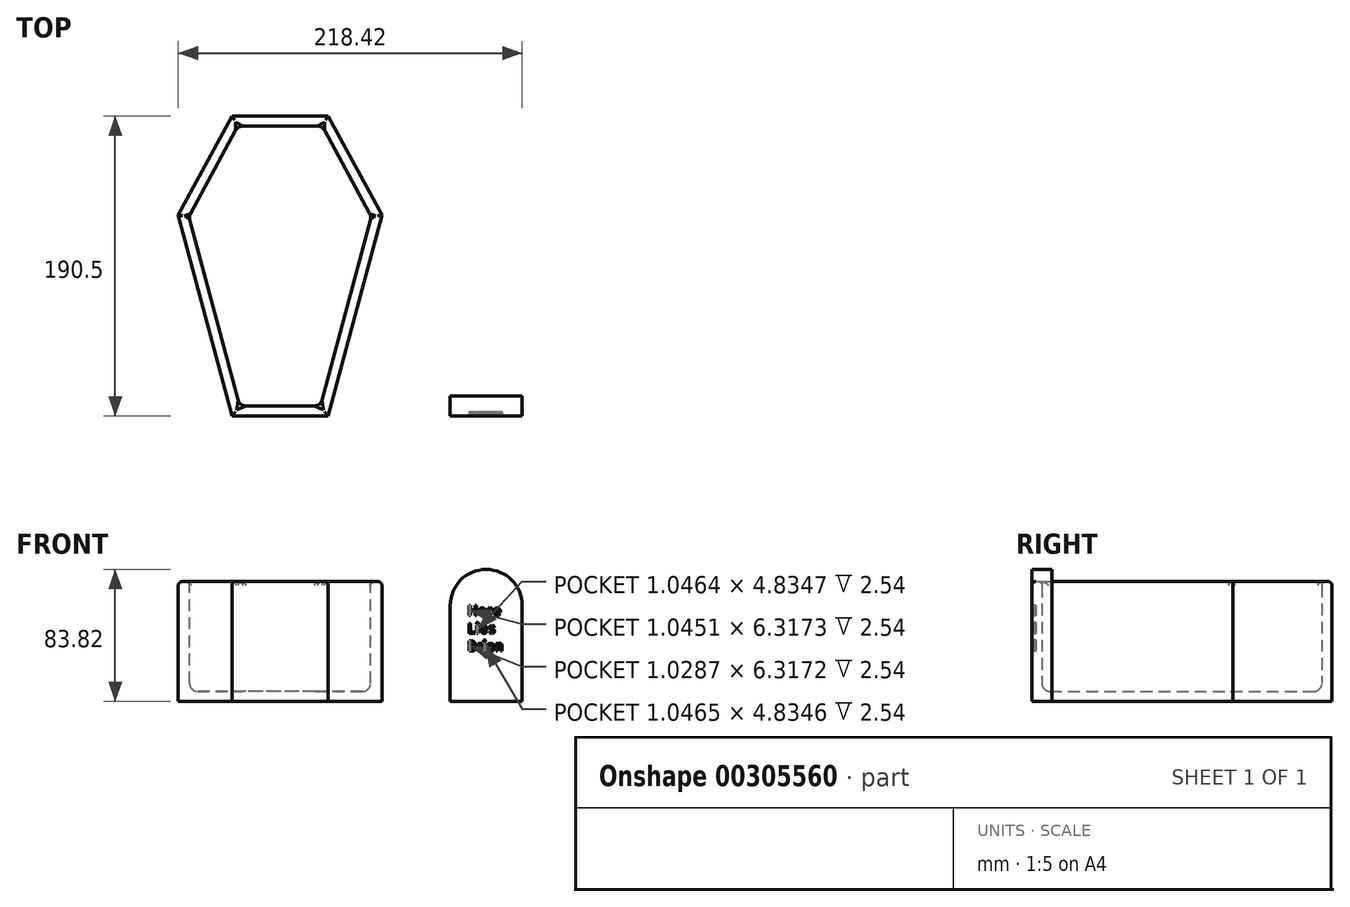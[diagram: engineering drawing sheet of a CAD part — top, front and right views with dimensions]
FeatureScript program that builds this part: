
annotation { "Feature Type Name" : "Feature", "Feature Type Description" : "" }
export const myFeature = defineFeature(function(context is Context, id is Id, definition is map)
    precondition{}
    {
        {
            var Q0;
            Q0=qCreatedBy(makeId("Top.planeOp"),FACE);
            var sketch = newSketch(context, id + "F0", { "sketchPlane" : qUnion([Q0])});
            skLineSegment(sketch, "E0", {"start": v(0, 0) * mm, "end": v(30.48, 0) * mm});
            skLineSegment(sketch, "E1", {"start": v(30.48, 0) * mm, "end": v(64.66, 127.58) * mm});
            skLineSegment(sketch, "E2", {"start": v(64.66, 127.58) * mm, "end": v(30.48, 190.5) * mm});
            skLineSegment(sketch, "E3", {"start": v(30.48, 190.5) * mm, "end": v(0, 190.5) * mm});
            skLineSegment(sketch, "E4.MirrorCS", {"start": v(-30.48, 190.5) * mm, "end": v(0, 190.5) * mm});
            skLineSegment(sketch, "E5.MirrorCS", {"start": v(-64.66, 127.58) * mm, "end": v(-30.48, 190.5) * mm});
            skLineSegment(sketch, "E6.MirrorCS", {"start": v(-30.48, 0) * mm, "end": v(-64.66, 127.58) * mm});
            skLineSegment(sketch, "E7.MirrorCS", {"start": v(0, 0) * mm, "end": v(-30.48, 0) * mm});
            skSolve(sketch);
        }
        {
            var Q0;
            Q0=makeQuery(id+"F0.imprint","IMPRINT",FACE,{"disambiguationData":[TD([[makeQuery(id+"F0.imprint","IMPRINT",EDGE,{"derivedFrom":sQuery(id+"F0.wireOp",EDGE,"E0")}),1.0]])]});
            extrude(context, id + "F1", {"entities" : qUnion([Q0]), "depth" : 76.2 * mm});
        }
        {
            var Q0;
            Q0=makeQuery(id+"F1.opExtrude","CAP_FACE",FACE,{"disambiguationData":[OSD([sQuery(id+"F0.wireOp",EDGE,"E0"),sQuery(id+"F0.wireOp",EDGE,"E1"),sQuery(id+"F0.wireOp",EDGE,"E2"),sQuery(id+"F0.wireOp",EDGE,"E3"),sQuery(id+"F0.wireOp",EDGE,"E4.MirrorCS"),sQuery(id+"F0.wireOp",EDGE,"E5.MirrorCS"),sQuery(id+"F0.wireOp",EDGE,"E6.MirrorCS"),sQuery(id+"F0.wireOp",EDGE,"E7.MirrorCS")])],"isStart":false});
            shell(context, id + "F2", {"entities" : qUnion([Q0]), "thickness" : 6.35 * mm});
        }
        {
            var Q0;
            Q0=makeQuery(id+"F1.opExtrude","CAP_FACE",FACE,{"disambiguationData":[OSD([sQuery(id+"F0.wireOp",EDGE,"E0"),sQuery(id+"F0.wireOp",EDGE,"E1"),sQuery(id+"F0.wireOp",EDGE,"E2"),sQuery(id+"F0.wireOp",EDGE,"E3"),sQuery(id+"F0.wireOp",EDGE,"E4.MirrorCS"),sQuery(id+"F0.wireOp",EDGE,"E5.MirrorCS"),sQuery(id+"F0.wireOp",EDGE,"E6.MirrorCS"),sQuery(id+"F0.wireOp",EDGE,"E7.MirrorCS")])],"isStart":false});
            fillet(context, id + "F3", {"entities" : qUnion([Q0]), "radius" : 2.54 * mm, "tangentPropagation" : true, "allowEdgeOverflow" : false});
        }
        {
            var Q0;
            Q0=makeQuery(id+"F2.opShell","OFFSET_FACE",FACE,{"disambiguationData":[OSD([sQuery(id+"F0.wireOp",EDGE,"E0"),sQuery(id+"F0.wireOp",EDGE,"E1"),sQuery(id+"F0.wireOp",EDGE,"E2"),sQuery(id+"F0.wireOp",EDGE,"E3"),sQuery(id+"F0.wireOp",EDGE,"E4.MirrorCS"),sQuery(id+"F0.wireOp",EDGE,"E5.MirrorCS"),sQuery(id+"F0.wireOp",EDGE,"E6.MirrorCS"),sQuery(id+"F0.wireOp",EDGE,"E7.MirrorCS")])]});
            var Q1;
            Q1=makeQuery(id+"F2.opShell","OFFSET_FACE",FACE,{"disambiguationData":[OSD([sQuery(id+"F0.wireOp",EDGE,"E3"),sQuery(id+"F0.wireOp",EDGE,"E4.MirrorCS")])]});
            var Q2;
            Q2=makeQuery(id+"F2.opShell","OFFSET_FACE",FACE,{"disambiguationData":[OSD([sQuery(id+"F0.wireOp",EDGE,"E6.MirrorCS")])]});
            var Q3;
            Q3=makeQuery(id+"F2.opShell","OFFSET_FACE",FACE,{"disambiguationData":[OSD([sQuery(id+"F0.wireOp",EDGE,"E5.MirrorCS")])]});
            var Q4;
            Q4=makeQuery(id+"F2.opShell","OFFSET_FACE",FACE,{"disambiguationData":[OSD([sQuery(id+"F0.wireOp",EDGE,"E1")])]});
            var Q5;
            Q5=makeQuery(id+"F2.opShell","OFFSET_FACE",FACE,{"disambiguationData":[OSD([sQuery(id+"F0.wireOp",EDGE,"E2")])]});
            var Q6;
            Q6=makeQuery(id+"F2.opShell","OFFSET_FACE",FACE,{"disambiguationData":[OSD([sQuery(id+"F0.wireOp",EDGE,"E0"),sQuery(id+"F0.wireOp",EDGE,"E7.MirrorCS")])]});
            fillet(context, id + "F4", {"entities" : qUnion([Q0, Q1, Q2, Q3, Q4, Q5, Q6]), "radius" : 5.08 * mm, "tangentPropagation" : true, "allowEdgeOverflow" : false});
        }
        {
            var Q0;
            Q0=qCreatedBy(makeId("Front.planeOp"),FACE);
            var sketch = newSketch(context, id + "F5", { "sketchPlane" : qUnion([Q0])});
            skLineSegment(sketch, "E8.bottom", {"start": v(108.04, 0) * mm, "end": v(153.76, 0) * mm});
            skLineSegment(sketch, "E8.left", {"start": v(108.04, 0) * mm, "end": v(108.04, 60.96) * mm});
            skLineSegment(sketch, "E8.right", {"start": v(153.76, 0) * mm, "end": v(153.76, 60.96) * mm});
            skArc(sketch, "E9", {"start": v(153.76, 60.96) * mm, "mid": v(130.9, 83.82) * mm, "end": v(108.04, 60.96) * mm});
            skSolve(sketch);
        }
        {
            var Q0;
            Q0=makeQuery(id+"F5.imprint","IMPRINT",FACE,{"disambiguationData":[TD([[makeQuery(id+"F5.imprint","IMPRINT",EDGE,{"derivedFrom":sQuery(id+"F5.wireOp",EDGE,"E8.bottom")}),1.0]])]});
            extrude(context, id + "F6", {"entities" : qUnion([Q0]), "oppositeDirection" : true, "depth" : 12.7 * mm});
        }
        {
            var Q0;
            Q0=makeQuery(id+"F6.opExtrude","CAP_FACE",FACE,{"disambiguationData":[OSD([sQuery(id+"F5.wireOp",EDGE,"E8.bottom"),sQuery(id+"F5.wireOp",EDGE,"E8.left"),sQuery(id+"F5.wireOp",EDGE,"E8.right"),sQuery(id+"F5.wireOp",EDGE,"E9")])],"isStart":true});
            var sketch = newSketch(context, id + "F7", { "sketchPlane" : qUnion([Q0])});
            skText(sketch, "E10", { "text": "Here\nLies\nBrian", "fontName": "AllertaStencil-Regular.ttf"});
            const initialGuessF7  = {"E10": [0.11912, 0.05453, 1, 0, 0.00632]};
            skSetInitialGuess(sketch, initialGuessF7);
            skSolve(sketch);
        }
        {
            var Q0;
            Q0 = qSketchRegion(id + "F7", true);
            var Q1;
            Q1 = qConstructionFilter(qBodyType(qCreatedBy(id + "F7" ,EDGE), BodyType.WIRE), ConstructionObject.NO);
            extrude(context, id + "F8", {"entities" : qUnion([Q0]), "operationType" : NewBodyOperationType.REMOVE, "surfaceEntities" : qUnion([Q1]), "oppositeDirection" : true, "depth" : 2.54 * mm});
        }
    });
